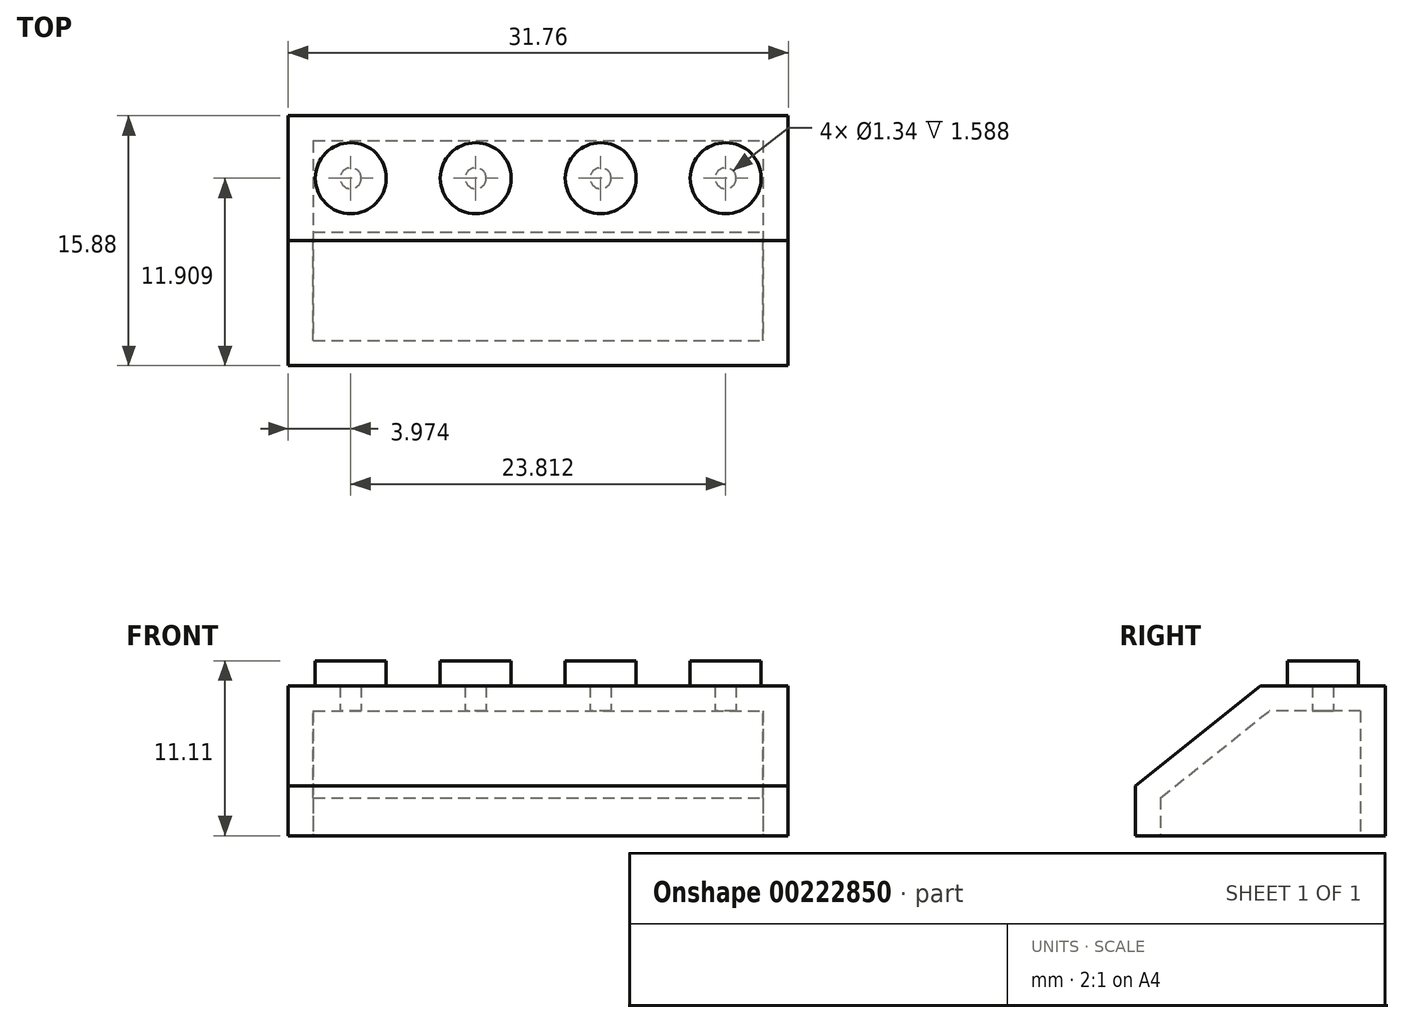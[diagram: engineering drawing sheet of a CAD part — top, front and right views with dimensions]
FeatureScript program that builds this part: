
annotation { "Feature Type Name" : "Feature", "Feature Type Description" : "" }
export const myFeature = defineFeature(function(context is Context, id is Id, definition is map)
    precondition{}
    {
        {
            var Q0;
            Q0=qCreatedBy(makeId("Top.planeOp"),FACE);
            var sketch = newSketch(context, id + "F0", { "sketchPlane" : qUnion([Q0])});
            skLineSegment(sketch, "E0.bottom", {"start": v(-15.88, 7.94) * mm, "end": v(15.88, 7.94) * mm});
            skLineSegment(sketch, "E0.top", {"start": v(-15.88, -7.94) * mm, "end": v(15.88, -7.94) * mm});
            skLineSegment(sketch, "E0.left", {"start": v(-15.88, 7.94) * mm, "end": v(-15.88, -7.94) * mm});
            skLineSegment(sketch, "E0.right", {"start": v(15.88, 7.94) * mm, "end": v(15.88, -7.94) * mm});
            skPoint(sketch, "E0.middle", {"position": v(0, 0) * mm});
            skCircle(sketch, "E1", {"center": v(-11.9, 3.97) * mm, "radius": 2.26 * mm});
            skCircle(sketch, "E2.1.0.0", {"center": v(-3.97, 3.97) * mm, "radius": 2.26 * mm});
            skLineSegment(sketch, "E2.direction1", {"start": v(-11.9, 3.97) * mm, "end": v(-3.97, 3.97) * mm, "construction": true});
            skLineSegment(sketch, "E2.direction2", {"start": v(-11.9, 3.97) * mm, "end": v(-11.9, -3.97) * mm, "construction": true});
            skCircle(sketch, "E3.0.2.0", {"center": v(3.97, 3.97) * mm, "radius": 2.26 * mm});
            skCircle(sketch, "E3.0.3.0", {"center": v(11.9, 3.97) * mm, "radius": 2.26 * mm});
            skSolve(sketch);
        }
        {
            var Q0;
            Q0=qSketchRegion(id+"F0",true);
            var Q1;
            Q1=makeQuery(id+"F0.imprint","IMPRINT",FACE,{"disambiguationData":[TD([[makeQuery(id+"F0.imprint","IMPRINT",EDGE,{"derivedFrom":sQuery(id+"F0.wireOp",EDGE,"ee4a0424-0ca1-48ee-9d31-a4736ef25bc9.0")}),1.0]])]});
            var Q2;
            Q2=makeQuery(id+"F0.imprint","IMPRINT",FACE,{"disambiguationData":[TD([[makeQuery(id+"F0.imprint","IMPRINT",EDGE,{"derivedFrom":sQuery(id+"F0.wireOp",EDGE,"WonEwQum-N0hj-o9Eq-pDde-ICulayySK2IP")}),1.0]])]});
            extrude(context, id + "F1", {"entities" : qUnion([Q0, Q1, Q2]), "depth" : 9.52 * mm});
        }
        {
            var Q0;
            Q0=makeQuery(id+"F0.imprint","IMPRINT",FACE,{"disambiguationData":[TD([[makeQuery(id+"F0.imprint","IMPRINT",EDGE,{"derivedFrom":sQuery(id+"F0.wireOp",EDGE,"E1")}),1.0]])]});
            var Q1;
            Q1=makeQuery(id+"F0.imprint","IMPRINT",FACE,{"disambiguationData":[TD([[makeQuery(id+"F0.imprint","IMPRINT",EDGE,{"derivedFrom":sQuery(id+"F0.wireOp",EDGE,"E2.1.0.0")}),1.0]])]});
            var Q2;
            Q2=makeQuery(id+"F0.imprint","IMPRINT",FACE,{"disambiguationData":[TD([[makeQuery(id+"F0.imprint","IMPRINT",EDGE,{"derivedFrom":sQuery(id+"F0.wireOp",EDGE,"E3.0.2.0")}),1.0]])]});
            var Q3;
            Q3=makeQuery(id+"F0.imprint","IMPRINT",FACE,{"disambiguationData":[TD([[makeQuery(id+"F0.imprint","IMPRINT",EDGE,{"derivedFrom":sQuery(id+"F0.wireOp",EDGE,"E3.0.3.0")}),1.0]])]});
            extrude(context, id + "F2", {"entities" : qUnion([Q0, Q1, Q2, Q3]), "operationType" : NewBodyOperationType.ADD, "depth" : 11.1 * mm});
        }
        {
            var Q0;
            Q0=makeQuery(id+"F1.opExtrude","SWEPT_FACE",FACE,{"disambiguationData":[OSD([sQuery(id+"F0.wireOp",EDGE,"E0.right")])]});
            var sketch = newSketch(context, id + "F3", { "sketchPlane" : qUnion([Q0])});
            skPoint(sketch, "E4", {"position": v(0, 9.53) * mm});
            skPoint(sketch, "E5", {"position": v(-7.94, 3.18) * mm});
            skLineSegment(sketch, "E6", {"start": v(-7.94, 3.17) * mm, "end": v(0, 9.53) * mm});
            skSolve(sketch);
        }
        {
            var Q0;
            {var subQ0=sQuery(id+"F3.wireOp",EDGE,"E6");Q0=makeQuery(id+"F3.imprint","IMPRINT",FACE,{"disambiguationData":[TD([[makeQuery(id+"F3.imprint","IMPRINT",EDGE,{"derivedFrom":subQ0}),1.0]])]});}
            extrude(context, id + "F4", {"entities" : qUnion([Q0]), "operationType" : NewBodyOperationType.REMOVE, "endBound" : BoundingType.THROUGH_ALL, "oppositeDirection" : true, "depth" : 25.4 * mm});
        }
        {
            var Q0;
            {var subQ0=sQuery(id+"F0.wireOp",EDGE,"E2.1.0.0");var subQ1=sQuery(id+"F0.wireOp",EDGE,"E1");Q0=makeQuery(id+"F2.boolean.opBoolean","MERGE",FACE,{"derivedFrom":[makeQuery(id+"F1.opExtrude","CAP_FACE",FACE,{"disambiguationData":[OSD([sQuery(id+"F0.wireOp",EDGE,"E0.bottom"),sQuery(id+"F0.wireOp",EDGE,"E0.top"),sQuery(id+"F0.wireOp",EDGE,"E0.left"),sQuery(id+"F0.wireOp",EDGE,"E0.right"),subQ1,subQ0])],"isStart":true}),makeQuery(id+"F2.opExtrude","CAP_FACE",FACE,{"disambiguationData":[OSD([subQ1])],"isStart":true}),makeQuery(id+"F2.opExtrude","CAP_FACE",FACE,{"disambiguationData":[OSD([subQ0])],"isStart":true})]});}
            shell(context, id + "F5", {"entities" : qUnion([Q0]), "thickness" : 1.59 * mm});
        }
    });
